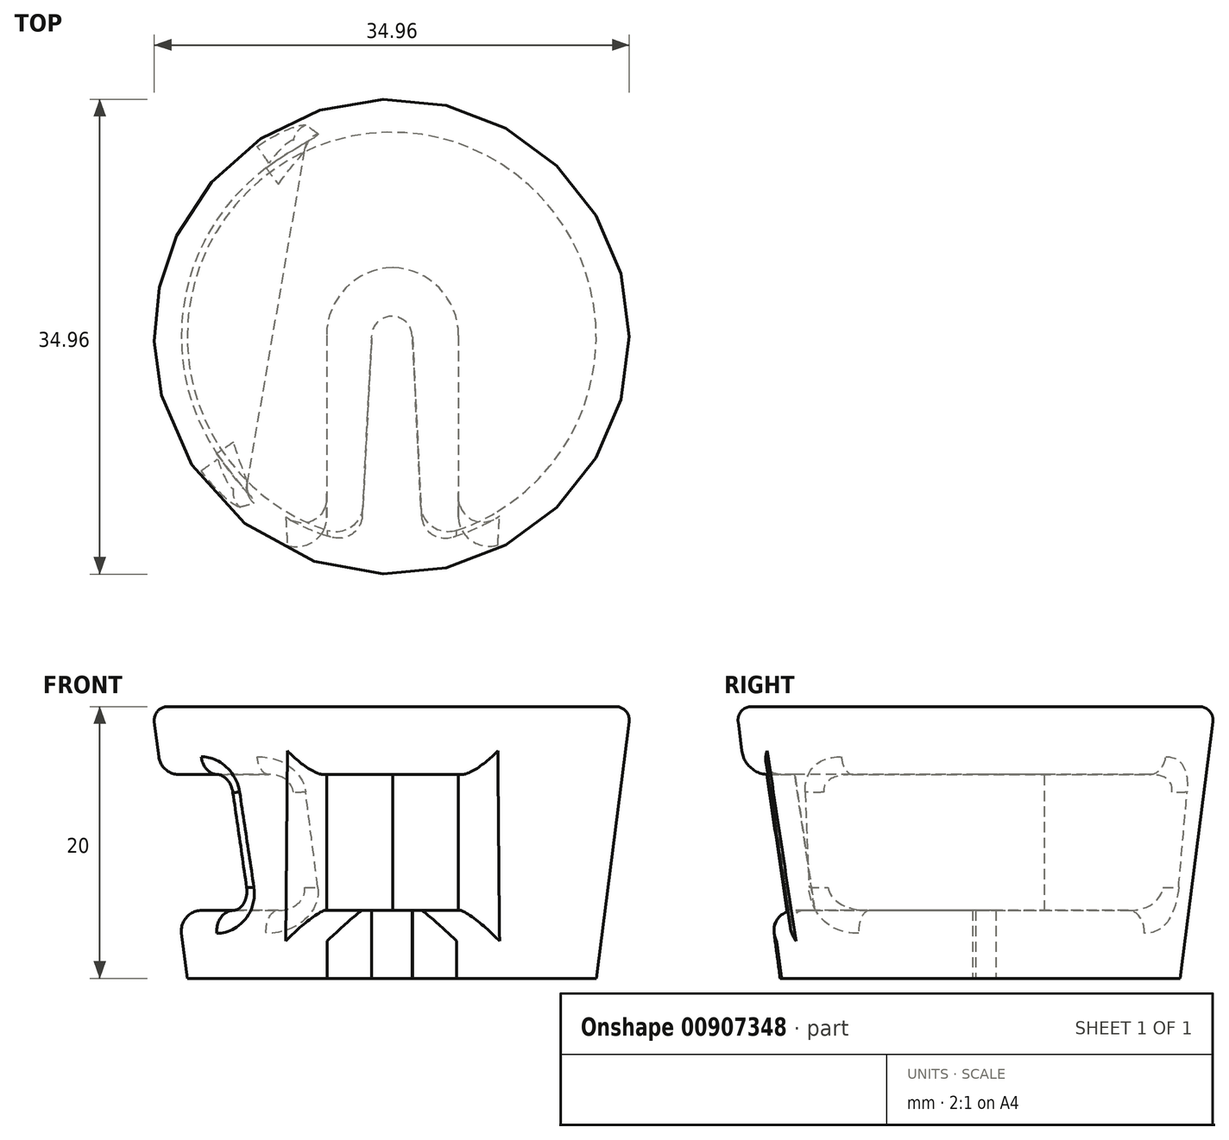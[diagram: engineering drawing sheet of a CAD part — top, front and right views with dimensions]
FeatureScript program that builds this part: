
annotation { "Feature Type Name" : "Feature", "Feature Type Description" : "" }
export const myFeature = defineFeature(function(context is Context, id is Id, definition is map)
    precondition{}
    {
        {
            var Q0;
            Q0=qCreatedBy(makeId("Top.planeOp"),FACE);
            var sketch = newSketch(context, id + "F0", { "sketchPlane" : qUnion([Q0])});
            skCircle(sketch, "E0", {"center": v(0, 0) * mm, "radius": 15.04 * mm});
            skSolve(sketch);
        }
        {
            var Q0;
            Q0=qCreatedBy(makeId("Top.planeOp"),FACE);
            cPlane(context, id + "F1", {"entities" : qUnion([Q0]), "cplaneType" : CPlaneType.OFFSET, "offset" : 20 * mm, "width" : 150 * mm, "height" : 150 * mm});
        }
        {
            var Q0;
            Q0=qCreatedBy(makeId("Top.planeOp"),FACE);
            cPlane(context, id + "F2", {"entities" : qUnion([Q0]), "cplaneType" : CPlaneType.OFFSET, "offset" : 5 * mm, "width" : 150 * mm, "height" : 150 * mm});
        }
        {
            var Q0;
            Q0=qCreatedBy(id+"F1.planeOp",FACE);
            var sketch = newSketch(context, id + "F3", { "sketchPlane" : qUnion([Q0])});
            skCircle(sketch, "E1", {"center": v(0, 0) * mm, "radius": 17.62 * mm});
            skSolve(sketch);
        }
        {
            var Q0;
            Q0=qCreatedBy(id+"F2.planeOp",FACE);
            var sketch = newSketch(context, id + "F4", { "sketchPlane" : qUnion([Q0])});
            skPoint(sketch, "E2", {"position": v(0, 0) * mm});
            skLineSegment(sketch, "E3.top", {"start": v(-3.91, -19.64) * mm, "end": v(4.91, -19.64) * mm});
            skLineSegment(sketch, "E4.bottom", {"start": v(-4.8, 5.1) * mm, "end": v(4.91, 5.1) * mm});
            skLineSegment(sketch, "E4.top", {"start": v(-4.8, -19.64) * mm, "end": v(4.91, -19.64) * mm});
            skLineSegment(sketch, "E4.left", {"start": v(-4.8, 5.1) * mm, "end": v(-4.8, -19.64) * mm});
            skLineSegment(sketch, "E4.right", {"start": v(4.91, 5.1) * mm, "end": v(4.91, -19.64) * mm});
            skSolve(sketch);
        }
        {
            var Q0;
            Q0 = qSketchRegion(id + "F0", true);
            var Q1;
            Q1 = qSketchRegion(id + "F3", true);
            loft(context, id + "F5", {"sheetProfilesArray" : [{ "sheetProfileEntities" : qUnion([Q0]) }, { "sheetProfileEntities" : qUnion([Q1]) }]});
        }
        {
            var Q0;
            Q0=qCreatedBy(makeId("Top.planeOp"),FACE);
            cPlane(context, id + "F6", {"entities" : qUnion([Q0]), "cplaneType" : CPlaneType.OFFSET, "offset" : 15 * mm, "width" : 150 * mm, "height" : 150 * mm});
        }
        {
            var Q0;
            Q0 = qSketchRegion(id + "F4", true);
            extrude(context, id + "F7", {"entities" : qUnion([Q0]), "operationType" : NewBodyOperationType.REMOVE, "depth" : 10 * mm, "offsetDistance" : 25 * mm});
        }
        {
            var Q0;
            Q0=qCreatedBy(makeId("Top.planeOp"),FACE);
            var sketch = newSketch(context, id + "F8", { "sketchPlane" : qUnion([Q0])});
            skLineSegment(sketch, "E5.top", {"start": v(2.5, -19.82) * mm, "end": v(-2.5, -19.82) * mm});
            skPoint(sketch, "E5.middle", {"position": v(0, -9.91) * mm});
            skLineSegment(sketch, "E6", {"start": v(2.5, -19.82) * mm, "end": v(1.53, 0) * mm});
            skLineSegment(sketch, "E7", {"start": v(1.53, 0) * mm, "end": v(-1.47, 0) * mm});
            skLineSegment(sketch, "E8", {"start": v(-1.47, 0) * mm, "end": v(-2.5, -19.82) * mm});
            skSolve(sketch);
        }
        {
            var Q0;
            Q0 = qSketchRegion(id + "F8", true);
            extrude(context, id + "F9", {"entities" : qUnion([Q0]), "operationType" : NewBodyOperationType.REMOVE, "depth" : 10 * mm, "offsetDistance" : 25 * mm});
        }
        {
            var Q0;
            Q0=qCreatedBy(makeId("Top.planeOp"),FACE);
            var sketch = newSketch(context, id + "F10", { "sketchPlane" : qUnion([Q0])});
            skPoint(sketch, "E9", {"position": v(0, 0) * mm});
            skSolve(sketch);
        }
        {
            var Q0;
            Q0=sQuery(id+"F10.wireOp",VERTEX,"E9");
            var Q1;
            Q1=makeQuery(id+"F5.opLoft","SWEPT_BODY",BODY,{"disambiguationData":[OSD([makeQuery(id+"F0.imprint","IMPRINT",FACE,{"disambiguationData":[TD([[makeQuery(id+"F0.imprint","IMPRINT",EDGE,{"derivedFrom":sQuery(id+"F0.wireOp",EDGE,"E0")}),1.0]])]}),makeQuery(id+"F3.imprint","IMPRINT",FACE,{"disambiguationData":[TD([[makeQuery(id+"F3.imprint","IMPRINT",EDGE,{"derivedFrom":sQuery(id+"F3.wireOp",EDGE,"E1")}),1.0]])]})])]});
            hole(context, id + "F11", {"style" : HoleStyle.SIMPLE, "endStyle" : HoleEndStyle.BLIND, "oppositeDirection" : true, "holeDiameter" : 3 * mm, "majorDiameter" : 5 * mm, "holeDepth" : 7 * mm, "isTappedThrough" : true, "tappedDepth" : 12 * mm, "tapClearance" : 3, "startFromSketch" : true, "locations" : qUnion([Q0]), "scope" : qUnion([Q1])});
        }
        {
            var Q0;
            Q0=makeQuery(id+"F7.boolean.opBoolean","COPY",EDGE,{"derivedFrom":makeQuery(id+"F7.opExtrude","SWEPT_EDGE",EDGE,{"disambiguationData":[OSD([sQuery(id+"F4.wireOp",EDGE,"E4.bottom"),sQuery(id+"F4.wireOp",EDGE,"E4.right")])]})});
            var Q1;
            Q1=makeQuery(id+"F7.boolean.opBoolean","COPY",EDGE,{"derivedFrom":makeQuery(id+"F7.opExtrude","SWEPT_EDGE",EDGE,{"disambiguationData":[OSD([sQuery(id+"F4.wireOp",EDGE,"E4.bottom"),sQuery(id+"F4.wireOp",EDGE,"E4.left")])]})});
            fillet(context, id + "F12", {"entities" : qUnion([Q0, Q1]), "radius" : 5 * mm, "tangentPropagation" : true, "allowEdgeOverflow" : false});
        }
        {
            var Q0;
            Q0=qCreatedBy(id+"F2.planeOp",FACE);
            var sketch = newSketch(context, id + "F13", { "sketchPlane" : qUnion([Q0])});
            skLineSegment(sketch, "E10", {"start": v(-10.98, -14.06) * mm, "end": v(-4.99, 20.6) * mm});
            skLineSegment(sketch, "E11", {"start": v(-4.99, 20.6) * mm, "end": v(-17.15, 20.6) * mm});
            skLineSegment(sketch, "E12", {"start": v(-17.15, 20.6) * mm, "end": v(-17.15, -14.06) * mm});
            skLineSegment(sketch, "E13", {"start": v(-17.15, -14.06) * mm, "end": v(-10.98, -14.06) * mm});
            skSolve(sketch);
        }
        {
            var Q0;
            Q0=qCreatedBy(id+"F6.planeOp",FACE);
            var sketch = newSketch(context, id + "F14", { "sketchPlane" : qUnion([Q0])});
            skLineSegment(sketch, "E14", {"start": v(-12.35, -14.1) * mm, "end": v(-6.36, 20.57) * mm});
            skLineSegment(sketch, "E15", {"start": v(-6.36, 20.57) * mm, "end": v(-17.1, 20.57) * mm});
            skLineSegment(sketch, "E16", {"start": v(-17.1, 20.57) * mm, "end": v(-17.1, -14.1) * mm});
            skLineSegment(sketch, "E17", {"start": v(-17.1, -14.1) * mm, "end": v(-12.35, -14.1) * mm});
            skSolve(sketch);
        }
        {
            var Q0;
            Q0 = qSketchRegion(id + "F13", true);
            var Q1;
            Q1 = qSketchRegion(id + "F14", true);
            loft(context, id + "F15", {"operationType" : NewBodyOperationType.REMOVE, "sheetProfilesArray" : [{ "sheetProfileEntities" : qUnion([Q0]) }, { "sheetProfileEntities" : qUnion([Q1]) }]});
        }
        {
            var Q0;
            Q0=makeQuery(id+"F15.boolean.opBoolean","INTERSECT",EDGE,{"derivedFrom":[makeQuery(id+"F5.opLoft","SWEPT_FACE",FACE,{"disambiguationData":[OSD([sQuery(id+"F0.wireOp",EDGE,"E0"),sQuery(id+"F3.wireOp",EDGE,"E1")])]}),makeQuery(id+"F15.opLoft","CAP_FACE",FACE,{"disambiguationData":[OSD([makeQuery(id+"F14.imprint","IMPRINT",FACE,{"disambiguationData":[TD([[makeQuery(id+"F14.imprint","IMPRINT",EDGE,{"derivedFrom":sQuery(id+"F14.wireOp",EDGE,"E14")}),1.0]])]})])],"isStart":true})]});
            var Q1;
            Q1=makeQuery(id+"F15.boolean.opBoolean","INTERSECT",EDGE,{"disambiguationData":[OD(1.0)],"derivedFrom":[makeQuery(id+"F5.opLoft","SWEPT_FACE",FACE,{"disambiguationData":[OSD([sQuery(id+"F0.wireOp",EDGE,"E0"),sQuery(id+"F3.wireOp",EDGE,"E1")])]}),makeQuery(id+"F15.opLoft","SWEPT_FACE",FACE,{"disambiguationData":[OSD([sQuery(id+"F13.wireOp",EDGE,"E10"),sQuery(id+"F13.wireOp",EDGE,"E11"),sQuery(id+"F13.wireOp",EDGE,"E13"),sQuery(id+"F14.wireOp",EDGE,"E14"),sQuery(id+"F14.wireOp",EDGE,"E15"),sQuery(id+"F14.wireOp",EDGE,"E17")])]})]});
            var Q2;
            Q2=makeQuery(id+"F15.boolean.opBoolean","INTERSECT",EDGE,{"derivedFrom":[makeQuery(id+"F5.opLoft","SWEPT_FACE",FACE,{"disambiguationData":[OSD([sQuery(id+"F0.wireOp",EDGE,"E0"),sQuery(id+"F3.wireOp",EDGE,"E1")])]}),makeQuery(id+"F15.opLoft","CAP_FACE",FACE,{"disambiguationData":[OSD([makeQuery(id+"F13.imprint","IMPRINT",FACE,{"disambiguationData":[TD([[makeQuery(id+"F13.imprint","IMPRINT",EDGE,{"derivedFrom":sQuery(id+"F13.wireOp",EDGE,"E10")}),1.0]])]})])],"isStart":true})]});
            var Q3;
            Q3=makeQuery(id+"F15.boolean.opBoolean","INTERSECT",EDGE,{"disambiguationData":[OD(0.0)],"derivedFrom":[makeQuery(id+"F5.opLoft","SWEPT_FACE",FACE,{"disambiguationData":[OSD([sQuery(id+"F0.wireOp",EDGE,"E0"),sQuery(id+"F3.wireOp",EDGE,"E1")])]}),makeQuery(id+"F15.opLoft","SWEPT_FACE",FACE,{"disambiguationData":[OSD([sQuery(id+"F13.wireOp",EDGE,"E10"),sQuery(id+"F13.wireOp",EDGE,"E11"),sQuery(id+"F13.wireOp",EDGE,"E13"),sQuery(id+"F14.wireOp",EDGE,"E14"),sQuery(id+"F14.wireOp",EDGE,"E15"),sQuery(id+"F14.wireOp",EDGE,"E17")])]})]});
            var Q4;
            Q4=makeQuery(id+"F15.boolean.opBoolean","COPY",EDGE,{"derivedFrom":makeQuery(id+"F15.opLoft","MID_CAP_EDGE",EDGE,{"disambiguationData":[OSD([sQuery(id+"F14.wireOp",EDGE,"E14"),sQuery(id+"F14.wireOp",EDGE,"E15"),sQuery(id+"F14.wireOp",EDGE,"E17")])],"capPos":1.0})});
            var Q5;
            Q5=makeQuery(id+"F15.boolean.opBoolean","COPY",EDGE,{"derivedFrom":makeQuery(id+"F15.opLoft","MID_CAP_EDGE",EDGE,{"disambiguationData":[OSD([sQuery(id+"F13.wireOp",EDGE,"E10"),sQuery(id+"F13.wireOp",EDGE,"E11"),sQuery(id+"F13.wireOp",EDGE,"E13")])],"capPos":0.0})});
            fillet(context, id + "F16", {"entities" : qUnion([Q0, Q1, Q2, Q3, Q4, Q5]), "radius" : 1.5 * mm, "tangentPropagation" : true, "allowEdgeOverflow" : false});
        }
        {
            var Q0;
            {var subQ0=makeQuery(id+"F5.opLoft","SWEPT_FACE",FACE,{"disambiguationData":[OSD([sQuery(id+"F0.wireOp",EDGE,"E0"),sQuery(id+"F3.wireOp",EDGE,"E1")])]});var subQ1=sQuery(id+"F4.wireOp",EDGE,"E4.right");var subQ2=makeQuery(id+"F7.opExtrude","CAP_FACE",FACE,{"disambiguationData":[OSD([sQuery(id+"F4.wireOp",EDGE,"E4.bottom"),sQuery(id+"F4.wireOp",EDGE,"E4.top"),sQuery(id+"F4.wireOp",EDGE,"E4.left"),subQ1])],"isStart":true});Q0=makeQuery(id+"F9.boolean.opBoolean","SPLIT",EDGE,{"disambiguationData":[TD([makeQuery(id+"F7.boolean.opBoolean","COPY",FACE,{"derivedFrom":makeQuery(id+"F7.opExtrude","SWEPT_FACE",FACE,{"disambiguationData":[OSD([subQ1])]})})])],"derivedFrom":makeQuery(id+"F7.boolean.opBoolean","INTERSECT",EDGE,{"derivedFrom":[subQ0,subQ2]})});}
            var Q1;
            {var subQ0=makeQuery(id+"F5.opLoft","SWEPT_FACE",FACE,{"disambiguationData":[OSD([sQuery(id+"F0.wireOp",EDGE,"E0"),sQuery(id+"F3.wireOp",EDGE,"E1")])]});var subQ1=sQuery(id+"F4.wireOp",EDGE,"E4.left");var subQ2=makeQuery(id+"F7.opExtrude","CAP_FACE",FACE,{"disambiguationData":[OSD([sQuery(id+"F4.wireOp",EDGE,"E4.bottom"),sQuery(id+"F4.wireOp",EDGE,"E4.top"),subQ1,sQuery(id+"F4.wireOp",EDGE,"E4.right")])],"isStart":true});Q1=makeQuery(id+"F9.boolean.opBoolean","SPLIT",EDGE,{"disambiguationData":[TD([makeQuery(id+"F7.boolean.opBoolean","COPY",FACE,{"derivedFrom":makeQuery(id+"F7.opExtrude","SWEPT_FACE",FACE,{"disambiguationData":[OSD([subQ1])]})})])],"derivedFrom":makeQuery(id+"F7.boolean.opBoolean","INTERSECT",EDGE,{"derivedFrom":[subQ0,subQ2]})});}
            var Q2;
            Q2=makeQuery(id+"F9.boolean.opBoolean","INTERSECT",EDGE,{"derivedFrom":[makeQuery(id+"F5.opLoft","SWEPT_FACE",FACE,{"disambiguationData":[OSD([sQuery(id+"F0.wireOp",EDGE,"E0"),sQuery(id+"F3.wireOp",EDGE,"E1")])]}),makeQuery(id+"F9.opExtrude","SWEPT_FACE",FACE,{"disambiguationData":[OSD([sQuery(id+"F8.wireOp",EDGE,"E6")])]})]});
            var Q3;
            Q3=makeQuery(id+"F9.boolean.opBoolean","INTERSECT",EDGE,{"derivedFrom":[makeQuery(id+"F5.opLoft","SWEPT_FACE",FACE,{"disambiguationData":[OSD([sQuery(id+"F0.wireOp",EDGE,"E0"),sQuery(id+"F3.wireOp",EDGE,"E1")])]}),makeQuery(id+"F9.opExtrude","SWEPT_FACE",FACE,{"disambiguationData":[OSD([sQuery(id+"F8.wireOp",EDGE,"E8")])]})]});
            var Q4;
            Q4=makeQuery(id+"F7.boolean.opBoolean","INTERSECT",EDGE,{"derivedFrom":[makeQuery(id+"F5.opLoft","SWEPT_FACE",FACE,{"disambiguationData":[OSD([sQuery(id+"F0.wireOp",EDGE,"E0"),sQuery(id+"F3.wireOp",EDGE,"E1")])]}),makeQuery(id+"F7.opExtrude","SWEPT_FACE",FACE,{"disambiguationData":[OSD([sQuery(id+"F4.wireOp",EDGE,"E4.left")])]})]});
            var Q5;
            Q5=makeQuery(id+"F7.boolean.opBoolean","INTERSECT",EDGE,{"derivedFrom":[makeQuery(id+"F5.opLoft","SWEPT_FACE",FACE,{"disambiguationData":[OSD([sQuery(id+"F0.wireOp",EDGE,"E0"),sQuery(id+"F3.wireOp",EDGE,"E1")])]}),makeQuery(id+"F7.opExtrude","SWEPT_FACE",FACE,{"disambiguationData":[OSD([sQuery(id+"F4.wireOp",EDGE,"E4.right")])]})]});
            var Q6;
            Q6=makeQuery(id+"F7.boolean.opBoolean","INTERSECT",EDGE,{"derivedFrom":[makeQuery(id+"F5.opLoft","SWEPT_FACE",FACE,{"disambiguationData":[OSD([sQuery(id+"F0.wireOp",EDGE,"E0"),sQuery(id+"F3.wireOp",EDGE,"E1")])]}),makeQuery(id+"F7.opExtrude","CAP_FACE",FACE,{"disambiguationData":[OSD([sQuery(id+"F4.wireOp",EDGE,"E4.bottom"),sQuery(id+"F4.wireOp",EDGE,"E4.top"),sQuery(id+"F4.wireOp",EDGE,"E4.left"),sQuery(id+"F4.wireOp",EDGE,"E4.right")])],"isStart":false})]});
            fillet(context, id + "F17", {"entities" : qUnion([Q0, Q1, Q2, Q3, Q4, Q5, Q6]), "radius" : 2 * mm, "tangentPropagation" : true, "allowEdgeOverflow" : false});
        }
        {
            var Q0;
            Q0=makeQuery(id+"F5.opLoft","CAP_FACE",FACE,{"disambiguationData":[OSD([makeQuery(id+"F3.imprint","IMPRINT",FACE,{"disambiguationData":[TD([[makeQuery(id+"F3.imprint","IMPRINT",EDGE,{"derivedFrom":sQuery(id+"F3.wireOp",EDGE,"E1")}),1.0]])]})])],"isStart":true});
            fillet(context, id + "F18", {"entities" : qUnion([Q0]), "radius" : 1 * mm, "tangentPropagation" : true, "allowEdgeOverflow" : false});
        }
    });
